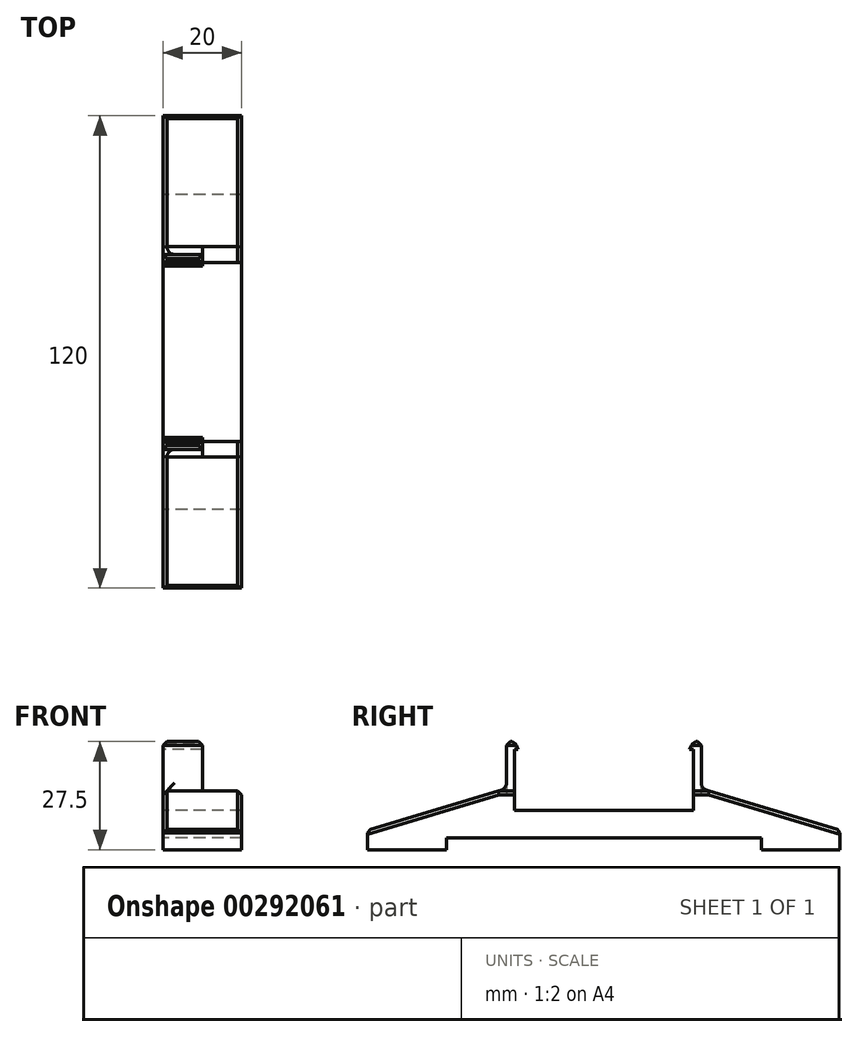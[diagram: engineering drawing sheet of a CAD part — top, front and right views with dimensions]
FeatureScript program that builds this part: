
annotation { "Feature Type Name" : "Feature", "Feature Type Description" : "" }
export const myFeature = defineFeature(function(context is Context, id is Id, definition is map)
    precondition{}
    {
        {
            var Q0;
            Q0=qCreatedBy(makeId("Right.planeOp"),FACE);
            var sketch = newSketch(context, id + "F0", { "sketchPlane" : qUnion([Q0])});
            skLineSegment(sketch, "E0", {"start": v(-22.75, 10) * mm, "end": v(22.75, 10) * mm});
            skLineSegment(sketch, "E1", {"start": v(22.75, 10) * mm, "end": v(22.75, 15) * mm});
            skLineSegment(sketch, "E2", {"start": v(-40, 3) * mm, "end": v(40, 3) * mm});
            skLineSegment(sketch, "E3", {"start": v(-40, 0) * mm, "end": v(-40, 3) * mm});
            skLineSegment(sketch, "E4", {"start": v(40, 3) * mm, "end": v(40, 0) * mm});
            skLineSegment(sketch, "E5", {"start": v(-22.75, 10) * mm, "end": v(-22.75, 15) * mm});
            skLineSegment(sketch, "E6.trimOffspring", {"start": v(40, 0) * mm, "end": v(60, 0) * mm});
            skLineSegment(sketch, "E7", {"start": v(60, 5) * mm, "end": v(60, 0) * mm});
            skLineSegment(sketch, "E8", {"start": v(26.75, 15) * mm, "end": v(22.75, 15) * mm});
            skLineSegment(sketch, "E9", {"start": v(26.75, 15) * mm, "end": v(60, 5) * mm});
            skLineSegment(sketch, "E10", {"start": v(-22.75, 15) * mm, "end": v(-26.75, 15) * mm});
            skLineSegment(sketch, "E11", {"start": v(-22.75, 15) * mm, "end": v(-22.75, 25.5) * mm});
            skLineSegment(sketch, "E12", {"start": v(-22.75, 25.5) * mm, "end": v(-21.75, 25.5) * mm});
            skLineSegment(sketch, "E13", {"start": v(-21.75, 25.5) * mm, "end": v(-22.75, 27.5) * mm});
            skLineSegment(sketch, "E14", {"start": v(-22.75, 27.5) * mm, "end": v(-24.75, 27.5) * mm});
            skLineSegment(sketch, "E15", {"start": v(-24.75, 27.5) * mm, "end": v(-24.75, 15) * mm});
            skLineSegment(sketch, "E16", {"start": v(24.75, 15) * mm, "end": v(24.75, 27.5) * mm});
            skLineSegment(sketch, "E17", {"start": v(22.75, 25.5) * mm, "end": v(21.75, 25.5) * mm});
            skLineSegment(sketch, "E18", {"start": v(22.75, 25.5) * mm, "end": v(22.75, 15) * mm});
            skLineSegment(sketch, "E19", {"start": v(21.75, 25.5) * mm, "end": v(22.75, 27.5) * mm});
            skLineSegment(sketch, "E20", {"start": v(22.75, 27.5) * mm, "end": v(24.75, 27.5) * mm});
            skLineSegment(sketch, "E21", {"start": v(-60, 5) * mm, "end": v(-60, 0) * mm});
            skLineSegment(sketch, "E22", {"start": v(-60, 0) * mm, "end": v(-40, 0) * mm});
            skLineSegment(sketch, "E23", {"start": v(-60, 5) * mm, "end": v(-26.75, 15) * mm});
            skSolve(sketch);
        }
        {
            var Q0;
            Q0=makeQuery(id+"F0.imprint","IMPRINT",FACE,{"disambiguationData":[TD([[makeQuery(id+"F0.imprint","IMPRINT",EDGE,{"derivedFrom":sQuery(id+"F0.wireOp",EDGE,"E0")}),-1.0]])]});
            var Q1;
            {var subQ0=sQuery(id+"F0.wireOp",EDGE,"E11");Q1=makeQuery(id+"F0.imprint","IMPRINT",FACE,{"disambiguationData":[TD([[makeQuery(id+"F0.imprint","IMPRINT",EDGE,{"derivedFrom":subQ0}),1.0]])]});}
            var Q2;
            {var subQ2=sQuery(id+"F0.wireOp",EDGE,"E16");Q2=makeQuery(id+"F0.imprint","IMPRINT",FACE,{"disambiguationData":[TD([[makeQuery(id+"F0.imprint","IMPRINT",EDGE,{"derivedFrom":subQ2}),1.0]])]});}
            extrude(context, id + "F1", {"entities" : qUnion([Q0, Q1, Q2]), "depth" : 10 * mm});
        }
        {
            var Q0;
            Q0=makeQuery(id+"F1.opExtrude","CAP_FACE",FACE,{"disambiguationData":[OSD([sQuery(id+"F0.wireOp",EDGE,"E0"),sQuery(id+"F0.wireOp",EDGE,"E1"),sQuery(id+"F0.wireOp",EDGE,"E2"),sQuery(id+"F0.wireOp",EDGE,"E3"),sQuery(id+"F0.wireOp",EDGE,"E4"),sQuery(id+"F0.wireOp",EDGE,"E5"),sQuery(id+"F0.wireOp",EDGE,"E6.trimOffspring"),sQuery(id+"F0.wireOp",EDGE,"E7"),sQuery(id+"F0.wireOp",EDGE,"E8"),sQuery(id+"F0.wireOp",EDGE,"E9"),sQuery(id+"F0.wireOp",EDGE,"E10"),sQuery(id+"F0.wireOp",EDGE,"E11"),sQuery(id+"F0.wireOp",EDGE,"E12"),sQuery(id+"F0.wireOp",EDGE,"E13"),sQuery(id+"F0.wireOp",EDGE,"E14"),sQuery(id+"F0.wireOp",EDGE,"E15"),sQuery(id+"F0.wireOp",EDGE,"E16"),sQuery(id+"F0.wireOp",EDGE,"E17"),sQuery(id+"F0.wireOp",EDGE,"E18"),sQuery(id+"F0.wireOp",EDGE,"E19"),sQuery(id+"F0.wireOp",EDGE,"E20"),sQuery(id+"F0.wireOp",EDGE,"E21"),sQuery(id+"F0.wireOp",EDGE,"E22"),sQuery(id+"F0.wireOp",EDGE,"E23")])],"isStart":false});
            var sketch = newSketch(context, id + "F2", { "sketchPlane" : qUnion([Q0])});
            skLineSegment(sketch, "E24", {"start": v(-24.75, 15) * mm, "end": v(-22.75, 15) * mm});
            skLineSegment(sketch, "E25", {"start": v(24.75, 15) * mm, "end": v(22.75, 15) * mm});
            skSolve(sketch);
        }
        {
            var Q0;
            {var subQ0=sQuery(id+"F2.wireOp",EDGE,"E24");Q0=makeQuery(id+"F2.imprint","IMPRINT",FACE,{"disambiguationData":[TD([[makeQuery(id+"F2.imprint","IMPRINT",EDGE,{"derivedFrom":subQ0}),-1.0]])]});}
            extrude(context, id + "F3", {"entities" : qUnion([Q0]), "operationType" : NewBodyOperationType.ADD, "depth" : 10 * mm});
        }
        {
            var Q0;
            Q0=makeQuery(id+"F1.opExtrude","SWEPT_EDGE",EDGE,{"disambiguationData":[OSD([sQuery(id+"F0.wireOp",EDGE,"E14"),sQuery(id+"F0.wireOp",EDGE,"E15")])]});
            var Q1;
            Q1=makeQuery(id+"F1.opExtrude","CAP_EDGE",EDGE,{"disambiguationData":[OSD([sQuery(id+"F0.wireOp",EDGE,"E14")])],"isStart":false});
            var Q2;
            Q2=makeQuery(id+"F1.opExtrude","SWEPT_EDGE",EDGE,{"disambiguationData":[OSD([sQuery(id+"F0.wireOp",EDGE,"E13"),sQuery(id+"F0.wireOp",EDGE,"E14")])]});
            var Q3;
            Q3=makeQuery(id+"F1.opExtrude","CAP_EDGE",EDGE,{"disambiguationData":[OSD([sQuery(id+"F0.wireOp",EDGE,"E14")])],"isStart":true});
            var Q4;
            Q4=makeQuery(id+"F1.opExtrude","SWEPT_EDGE",EDGE,{"disambiguationData":[OSD([sQuery(id+"F0.wireOp",EDGE,"E19"),sQuery(id+"F0.wireOp",EDGE,"E20")])]});
            var Q5;
            Q5=makeQuery(id+"F1.opExtrude","CAP_EDGE",EDGE,{"disambiguationData":[OSD([sQuery(id+"F0.wireOp",EDGE,"E20")])],"isStart":false});
            var Q6;
            Q6=makeQuery(id+"F1.opExtrude","SWEPT_EDGE",EDGE,{"disambiguationData":[OSD([sQuery(id+"F0.wireOp",EDGE,"E16"),sQuery(id+"F0.wireOp",EDGE,"E20")])]});
            var Q7;
            Q7=makeQuery(id+"F1.opExtrude","CAP_EDGE",EDGE,{"disambiguationData":[OSD([sQuery(id+"F0.wireOp",EDGE,"E20")])],"isStart":true});
            var Q8;
            Q8=makeQuery(id+"F3.opExtrude","CAP_EDGE",EDGE,{"disambiguationData":[OSD([sQuery(id+"F0.wireOp",EDGE,"E9")])],"isStart":false});
            var Q9;
            {var subQ0=sQuery(id+"F0.wireOp",EDGE,"E9");var subQ1=sQuery(id+"F0.wireOp",EDGE,"E7");Q9=makeQuery(id+"F3.boolean.opBoolean","MERGE",EDGE,{"derivedFrom":[makeQuery(id+"F1.opExtrude","SWEPT_EDGE",EDGE,{"disambiguationData":[OSD([subQ1,subQ0])]}),makeQuery(id+"F3.opExtrude","SWEPT_EDGE",EDGE,{"disambiguationData":[OSD([subQ1,subQ0])]})]});}
            var Q10;
            Q10=makeQuery(id+"F3.opExtrude","CAP_EDGE",EDGE,{"disambiguationData":[OSD([sQuery(id+"F0.wireOp",EDGE,"E8"),sQuery(id+"F2.wireOp",EDGE,"E25")])],"isStart":false});
            var Q11;
            Q11=makeQuery(id+"F3.opExtrude","CAP_EDGE",EDGE,{"disambiguationData":[OSD([sQuery(id+"F0.wireOp",EDGE,"E23")])],"isStart":false});
            var Q12;
            Q12=makeQuery(id+"F3.opExtrude","CAP_EDGE",EDGE,{"disambiguationData":[OSD([sQuery(id+"F0.wireOp",EDGE,"E10"),sQuery(id+"F2.wireOp",EDGE,"E24")])],"isStart":false});
            var Q13;
            {var subQ0=sQuery(id+"F0.wireOp",EDGE,"E23");var subQ1=sQuery(id+"F0.wireOp",EDGE,"E21");Q13=makeQuery(id+"F3.boolean.opBoolean","MERGE",EDGE,{"derivedFrom":[makeQuery(id+"F1.opExtrude","SWEPT_EDGE",EDGE,{"disambiguationData":[OSD([subQ1,subQ0])]}),makeQuery(id+"F3.opExtrude","SWEPT_EDGE",EDGE,{"disambiguationData":[OSD([subQ1,subQ0])]})]});}
            var Q14;
            Q14=makeQuery(id+"F1.opExtrude","CAP_EDGE",EDGE,{"disambiguationData":[OSD([sQuery(id+"F0.wireOp",EDGE,"E23")])],"isStart":true});
            var Q15;
            Q15=makeQuery(id+"F1.opExtrude","CAP_EDGE",EDGE,{"disambiguationData":[OSD([sQuery(id+"F0.wireOp",EDGE,"E10")])],"isStart":true});
            var Q16;
            Q16=makeQuery(id+"F1.opExtrude","CAP_EDGE",EDGE,{"disambiguationData":[OSD([sQuery(id+"F0.wireOp",EDGE,"E9")])],"isStart":true});
            var Q17;
            Q17=makeQuery(id+"F1.opExtrude","CAP_EDGE",EDGE,{"disambiguationData":[OSD([sQuery(id+"F0.wireOp",EDGE,"E8")])],"isStart":true});
            chamfer(context, id + "F4", {"entities" : qUnion([Q0, Q1, Q2, Q3, Q4, Q5, Q6, Q7, Q8, Q9, Q10, Q11, Q12, Q13, Q14, Q15, Q16, Q17]), "width" : 1 * mm, "tangentPropagation" : true});
        }
        {
            var Q0;
            Q0=makeQuery(id+"F1.opExtrude","SWEPT_EDGE",EDGE,{"disambiguationData":[OSD([sQuery(id+"F0.wireOp",EDGE,"E10"),sQuery(id+"F0.wireOp",EDGE,"E15")])]});
            var Q1;
            Q1=makeQuery(id+"F1.opExtrude","SWEPT_EDGE",EDGE,{"disambiguationData":[OSD([sQuery(id+"F0.wireOp",EDGE,"E8"),sQuery(id+"F0.wireOp",EDGE,"E16")])]});
            fillet(context, id + "F5", {"entities" : qUnion([Q0, Q1]), "radius" : 2 * mm, "tangentPropagation" : true, "allowEdgeOverflow" : false});
        }
    });
